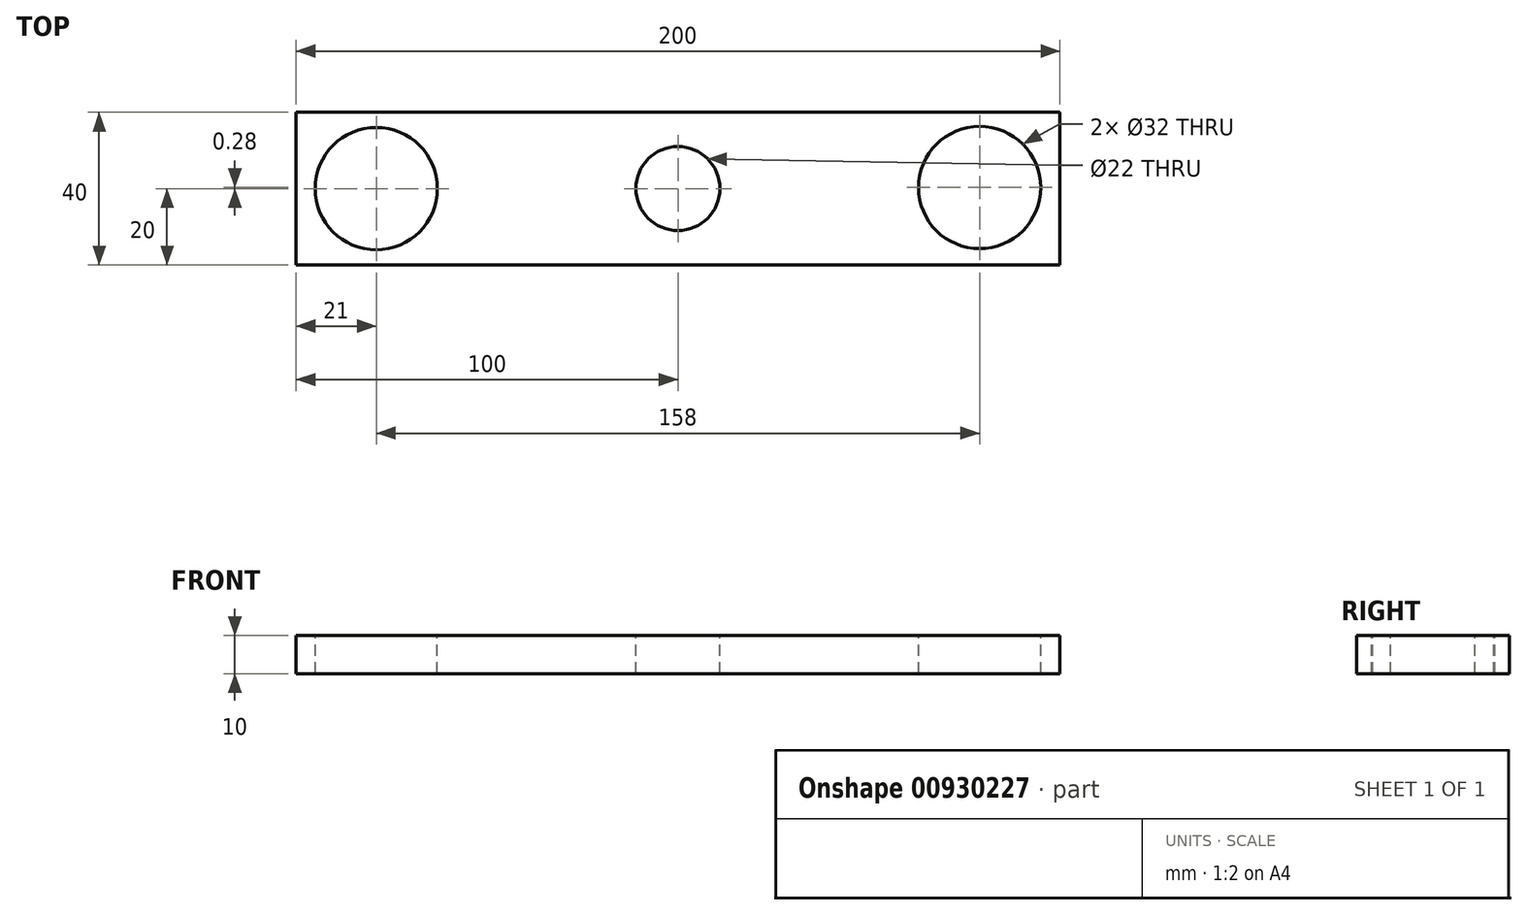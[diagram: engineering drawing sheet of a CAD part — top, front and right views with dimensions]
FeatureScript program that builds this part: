
annotation { "Feature Type Name" : "Feature", "Feature Type Description" : "" }
export const myFeature = defineFeature(function(context is Context, id is Id, definition is map)
    precondition{}
    {
        {
            var Q0;
            Q0=qCreatedBy(makeId("Top.planeOp"),FACE);
            var sketch = newSketch(context, id + "F0", { "sketchPlane" : qUnion([Q0])});
            skLineSegment(sketch, "E0.bottom", {"start": v(100, -20) * mm, "end": v(-100, -20) * mm});
            skLineSegment(sketch, "E0.top", {"start": v(100, 20) * mm, "end": v(-100, 20) * mm});
            skLineSegment(sketch, "E0.left", {"start": v(100, -20) * mm, "end": v(100, 20) * mm});
            skLineSegment(sketch, "E0.right", {"start": v(-100, -20) * mm, "end": v(-100, 20) * mm});
            skPoint(sketch, "E0.middle", {"position": v(0, 0) * mm});
            skSolve(sketch);
        }
        {
            var Q0;
            Q0=makeQuery(id+"F0.imprint","IMPRINT",FACE,{"disambiguationData":[TD([[makeQuery(id+"F0.imprint","IMPRINT",EDGE,{"derivedFrom":sQuery(id+"F0.wireOp",EDGE,"E0.bottom")}),-1.0]])]});
            extrude(context, id + "F1", {"entities" : qUnion([Q0]), "depth" : 10 * mm, "offsetDistance" : 25 * mm});
        }
        {
            var Q0;
            Q0=makeQuery(id+"F1.opExtrude","CAP_FACE",FACE,{"disambiguationData":[OSD([sQuery(id+"F0.wireOp",EDGE,"E0.bottom"),sQuery(id+"F0.wireOp",EDGE,"E0.top"),sQuery(id+"F0.wireOp",EDGE,"E0.left"),sQuery(id+"F0.wireOp",EDGE,"E0.right")])],"isStart":false});
            var sketch = newSketch(context, id + "F2", { "sketchPlane" : qUnion([Q0])});
            skCircle(sketch, "E1", {"center": v(-79, 0) * mm, "radius": 16 * mm});
            skLineSegment(sketch, "E2.0", {"start": v(100, -20) * mm, "end": v(-100, -20) * mm});
            skLineSegment(sketch, "E3", {"start": v(-100, 0) * mm, "end": v(-79, 0) * mm, "construction": true});
            skCircle(sketch, "E4", {"center": v(79, 0.28) * mm, "radius": 16 * mm});
            skLineSegment(sketch, "E5", {"start": v(100, 0.28) * mm, "end": v(79, 0.28) * mm});
            skCircle(sketch, "E6", {"center": v(0, 0) * mm, "radius": 11 * mm});
            skSolve(sketch);
        }
        {
            var Q0;
            Q0=qSketchRegion(id+"F2",true);
            extrude(context, id + "F3", {"entities" : qUnion([Q0]), "operationType" : NewBodyOperationType.REMOVE, "oppositeDirection" : true, "depth" : 10 * mm, "offsetDistance" : 25 * mm});
        }
    });
